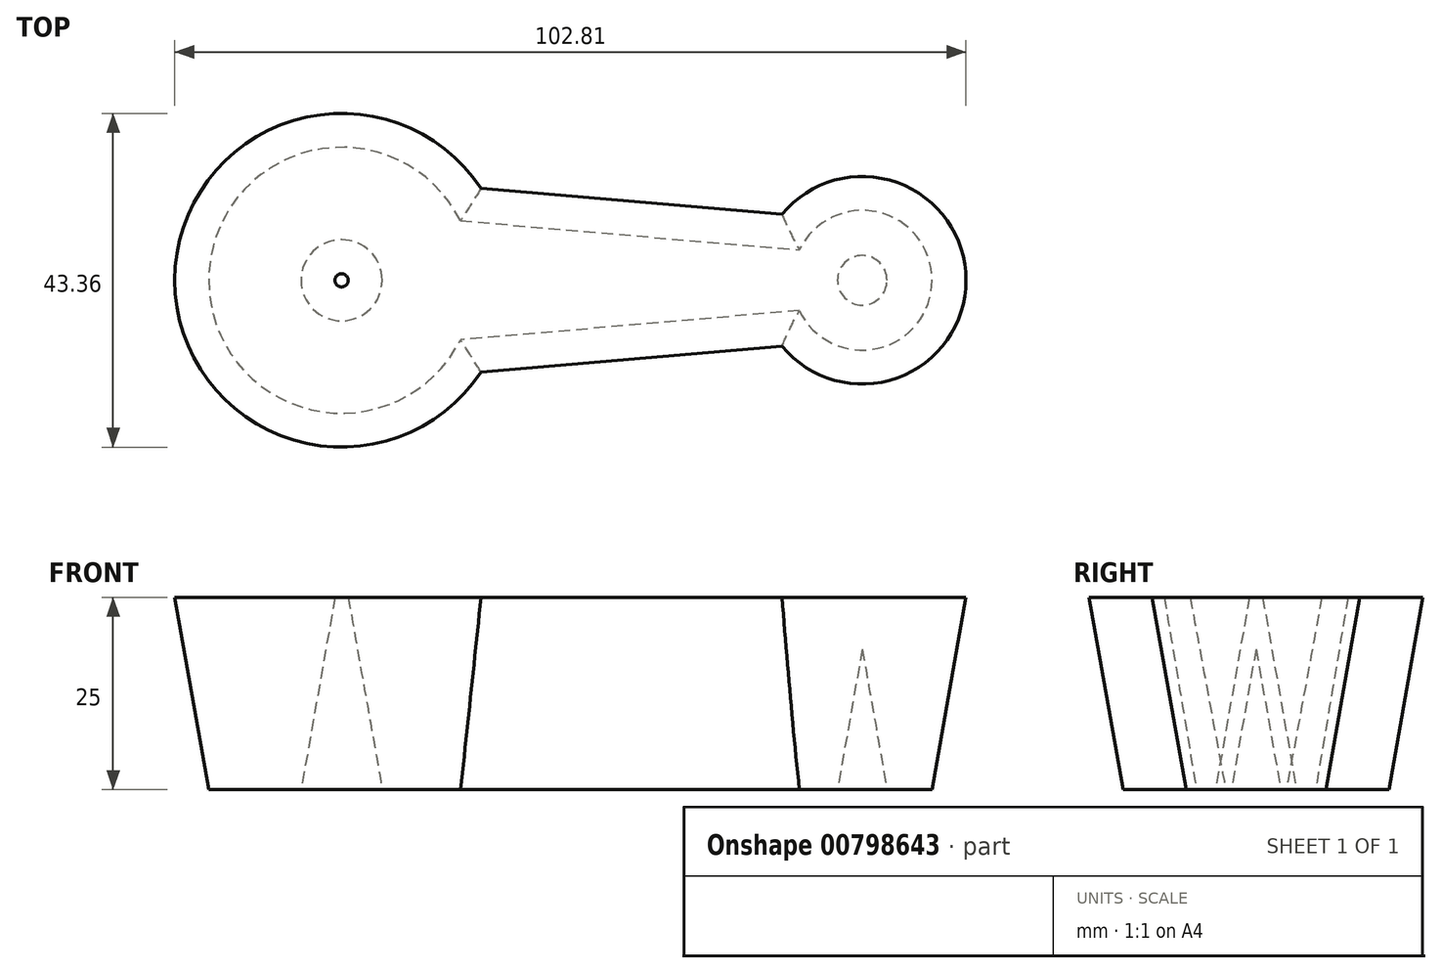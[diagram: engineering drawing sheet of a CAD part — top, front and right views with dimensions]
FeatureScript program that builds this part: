
annotation { "Feature Type Name" : "Feature", "Feature Type Description" : "" }
export const myFeature = defineFeature(function(context is Context, id is Id, definition is map)
    precondition{}
    {
        {
            var Q0;
            Q0=qCreatedBy(makeId("Top.planeOp"),FACE);
            var sketch = newSketch(context, id + "F0", { "sketchPlane" : qUnion([Q0])});
            skCircle(sketch, "E0", {"center": v(0, 0) * mm, "radius": 17.27 * mm});
            skCircle(sketch, "E1", {"center": v(67.65, 0) * mm, "radius": 9.07 * mm});
            skLineSegment(sketch, "E2", {"start": v(0, 0) * mm, "end": v(67.65, 0) * mm});
            skLineSegment(sketch, "E3", {"start": v(15.44, 7.74) * mm, "end": v(59.47, 3.94) * mm});
            skLineSegment(sketch, "E4.MirrorCS", {"start": v(15.44, -7.74) * mm, "end": v(59.47, -3.94) * mm});
            skCircle(sketch, "E5", {"center": v(0, 0) * mm, "radius": 5.27 * mm});
            skCircle(sketch, "E6", {"center": v(67.65, 0) * mm, "radius": 3.22 * mm});
            skSolve(sketch);
        }
        {
            var Q0;
            Q0 = qSketchRegion(id + "F0", true);
            extrude(context, id + "F1", {"entities" : qUnion([Q0]), "depth" : 25 * mm, "offsetDistance" : 25 * mm, "hasDraft" : true, "draftAngle" : 10 * degree});
        }
    });
